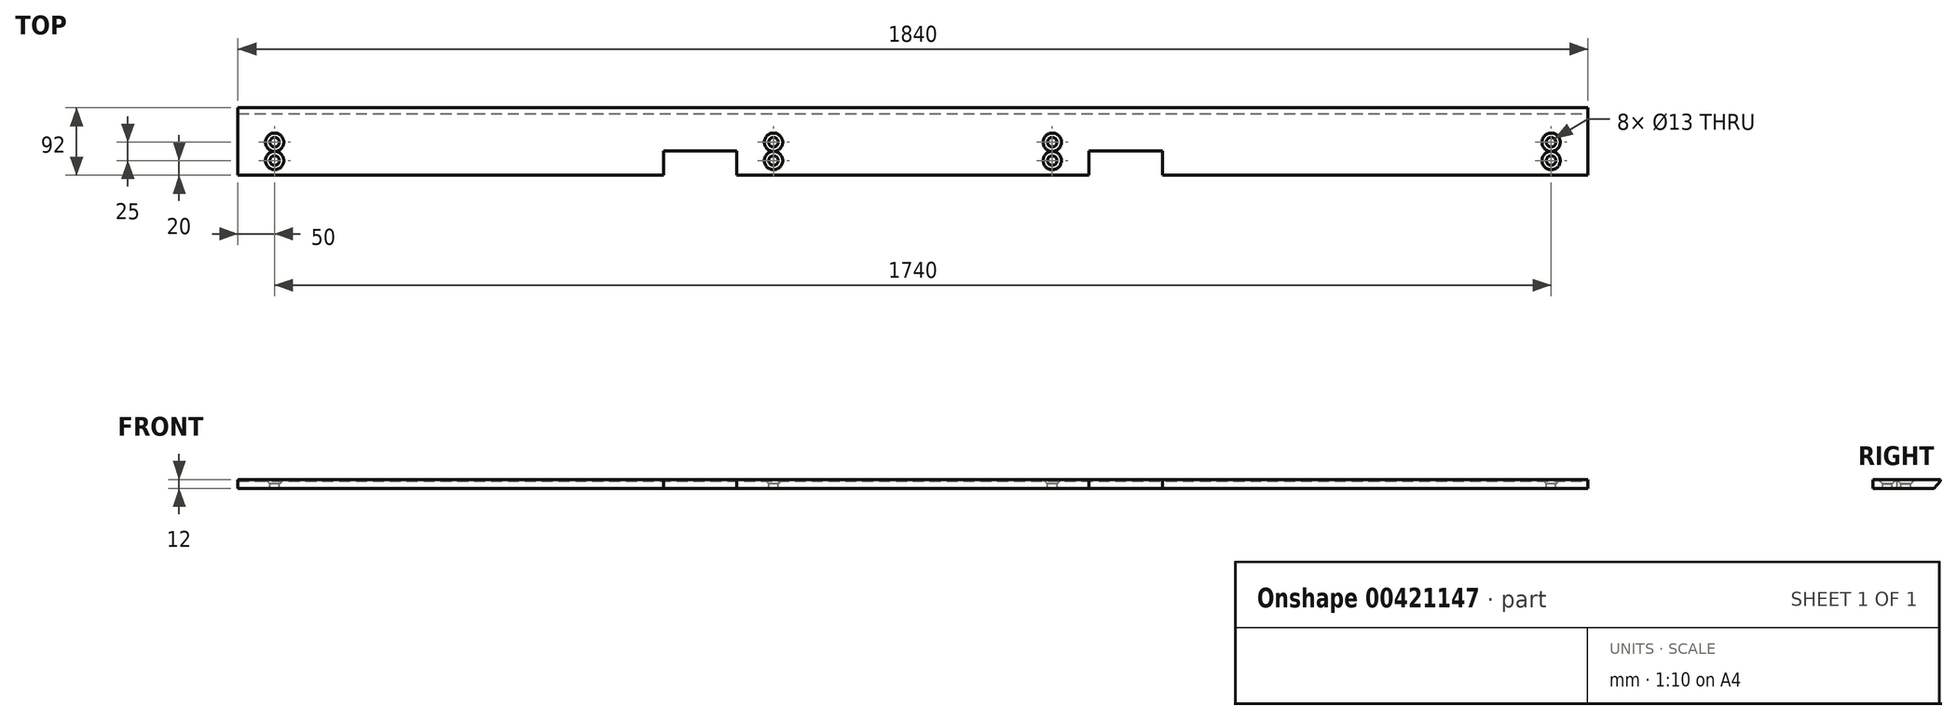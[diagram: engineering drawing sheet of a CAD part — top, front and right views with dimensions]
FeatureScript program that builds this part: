
annotation { "Feature Type Name" : "Feature", "Feature Type Description" : "" }
export const myFeature = defineFeature(function(context is Context, id is Id, definition is map)
    precondition{}
    {
        {
            var Q0;
            Q0=qCreatedBy(makeId("Top.planeOp"),FACE);
            var sketch = newSketch(context, id + "F0", { "sketchPlane" : qUnion([Q0])});
            skLineSegment(sketch, "E0.bottom", {"start": v(-920, 46) * mm, "end": v(920, 46) * mm});
            skLineSegment(sketch, "E0.top", {"start": v(-920, -46) * mm, "end": v(920, -46) * mm});
            skLineSegment(sketch, "E0.left", {"start": v(-920, 46) * mm, "end": v(-920, -46) * mm});
            skLineSegment(sketch, "E0.right", {"start": v(920, 46) * mm, "end": v(920, -46) * mm});
            skPoint(sketch, "E0.middle", {"position": v(0, 0) * mm});
            skSolve(sketch);
        }
        {
            var Q0;
            Q0=qSketchRegion(id+"F0",true);
            extrude(context, id + "F1", {"entities" : qUnion([Q0]), "endBound" : BoundingType.SYMMETRIC, "depth" : 12 * mm});
        }
        {
            var Q0;
            Q0=makeQuery(id+"F1.opExtrude","CAP_FACE",FACE,{"disambiguationData":[OSD([sQuery(id+"F0.wireOp",EDGE,"E0.bottom"),sQuery(id+"F0.wireOp",EDGE,"E0.top"),sQuery(id+"F0.wireOp",EDGE,"E0.left"),sQuery(id+"F0.wireOp",EDGE,"E0.right")])],"isStart":false});
            var sketch = newSketch(context, id + "F2", { "sketchPlane" : qUnion([Q0])});
            skLineSegment(sketch, "E1", {"start": v(0, 310.06) * mm, "end": v(0, -210.81) * mm, "construction": true});
            skLineSegment(sketch, "E2.0", {"start": v(-920, -46) * mm, "end": v(920, -46) * mm, "construction": true});
            skLineSegment(sketch, "E3.0", {"start": v(-240, 310.06) * mm, "end": v(-240, -210.81) * mm, "construction": true});
            skLineSegment(sketch, "E4.bottom", {"start": v(-240, -46) * mm, "end": v(-340, -46) * mm});
            skLineSegment(sketch, "E4.top", {"start": v(-240, -13) * mm, "end": v(-340, -13) * mm});
            skLineSegment(sketch, "E4.left", {"start": v(-240, -46) * mm, "end": v(-240, -13) * mm});
            skLineSegment(sketch, "E4.right", {"start": v(-340, -46) * mm, "end": v(-340, -13) * mm});
            skLineSegment(sketch, "E5.MirrorCS", {"start": v(340, -46) * mm, "end": v(340, -13) * mm});
            skLineSegment(sketch, "E6.MirrorCS", {"start": v(240, -46) * mm, "end": v(240, -13) * mm});
            skLineSegment(sketch, "E7.MirrorCS", {"start": v(240, -13) * mm, "end": v(340, -13) * mm});
            skLineSegment(sketch, "E8.MirrorCS", {"start": v(240, -46) * mm, "end": v(340, -46) * mm});
            skSolve(sketch);
        }
        {
            var Q0;
            Q0=qSketchRegion(id+"F2",true);
            extrude(context, id + "F3", {"entities" : qUnion([Q0]), "operationType" : NewBodyOperationType.REMOVE, "endBound" : BoundingType.THROUGH_ALL, "oppositeDirection" : true, "depth" : 25 * mm});
        }
        {
            var Q0;
            Q0=makeQuery(id+"F1.opExtrude","SWEPT_FACE",FACE,{"disambiguationData":[OSD([sQuery(id+"F0.wireOp",EDGE,"E0.right")])]});
            var sketch = newSketch(context, id + "F4", { "sketchPlane" : qUnion([Q0])});
            skLineSegment(sketch, "E9.0", {"start": v(46, 6) * mm, "end": v(-46, 6) * mm, "construction": true});
            skLineSegment(sketch, "E10.0", {"start": v(46, 4) * mm, "end": v(-46, 4) * mm, "construction": true});
            skLineSegment(sketch, "E11.0", {"start": v(46, 6) * mm, "end": v(46, -6) * mm, "construction": true});
            skLineSegment(sketch, "E12", {"start": v(46, 4) * mm, "end": v(37.6, -6) * mm});
            skLineSegment(sketch, "E13", {"start": v(46, 4) * mm, "end": v(46, -6) * mm});
            skLineSegment(sketch, "E14", {"start": v(46, -6) * mm, "end": v(37.6, -6) * mm});
            skSolve(sketch);
        }
        {
            var Q0;
            Q0=qSketchRegion(id+"F4",true);
            extrude(context, id + "F5", {"entities" : qUnion([Q0]), "operationType" : NewBodyOperationType.REMOVE, "endBound" : BoundingType.THROUGH_ALL, "oppositeDirection" : true, "depth" : 25 * mm});
        }
        {
            var Q0;
            Q0=makeQuery(id+"F1.opExtrude","CAP_FACE",FACE,{"disambiguationData":[OSD([sQuery(id+"F0.wireOp",EDGE,"E0.bottom"),sQuery(id+"F0.wireOp",EDGE,"E0.top"),sQuery(id+"F0.wireOp",EDGE,"E0.left"),sQuery(id+"F0.wireOp",EDGE,"E0.right")])],"isStart":false});
            var sketch = newSketch(context, id + "F6", { "sketchPlane" : qUnion([Q0])});
            skLineSegment(sketch, "E15", {"start": v(0, 160.59) * mm, "end": v(0, -190.3) * mm, "construction": true});
            skLineSegment(sketch, "E16.0", {"start": v(-190, 160.59) * mm, "end": v(-190, -190.3) * mm, "construction": true});
            skLineSegment(sketch, "E17.0", {"start": v(-870, 160.59) * mm, "end": v(-870, -190.3) * mm, "construction": true});
            skLineSegment(sketch, "E18.0", {"start": v(-920, -46) * mm, "end": v(0, -46) * mm, "construction": true});
            skPoint(sketch, "E19.orphan", {"position": v(-340, -46) * mm});
            skLineSegment(sketch, "E20.0", {"start": v(-920, -26) * mm, "end": v(0, -26) * mm, "construction": true});
            skLineSegment(sketch, "E21.0", {"start": v(-920, -1) * mm, "end": v(0, -1) * mm, "construction": true});
            skPoint(sketch, "E22", {"position": v(-870, -1) * mm});
            skPoint(sketch, "E23", {"position": v(-870, -26) * mm});
            skPoint(sketch, "E24", {"position": v(-190, -1) * mm});
            skPoint(sketch, "E25", {"position": v(-190, -26) * mm});
            skPoint(sketch, "E26.MirrorP", {"position": v(870, -1) * mm});
            skPoint(sketch, "E27.MirrorP", {"position": v(870, -26) * mm});
            skPoint(sketch, "E28.MirrorP", {"position": v(190, -1) * mm});
            skPoint(sketch, "E29.MirrorP", {"position": v(190, -26) * mm});
            skSolve(sketch);
        }
        {
            var Q0;
            Q0=sQuery(id+"F6.wireOp",VERTEX,"E22");
            var Q1;
            Q1=sQuery(id+"F6.wireOp",VERTEX,"E23");
            var Q2;
            Q2=sQuery(id+"F6.wireOp",VERTEX,"E24");
            var Q3;
            Q3=sQuery(id+"F6.wireOp",VERTEX,"E25");
            var Q4;
            Q4=sQuery(id+"F6.wireOp",VERTEX,"E29.MirrorP");
            var Q5;
            Q5=sQuery(id+"F6.wireOp",VERTEX,"E28.MirrorP");
            var Q6;
            Q6=sQuery(id+"F6.wireOp",VERTEX,"E26.MirrorP");
            var Q7;
            Q7=sQuery(id+"F6.wireOp",VERTEX,"E27.MirrorP");
            var Q8;
            Q8=makeQuery(id+"F1.opExtrude","SWEPT_BODY",BODY,{"disambiguationData":[OSD([sQuery(id+"F0.wireOp",EDGE,"E0.bottom"),sQuery(id+"F0.wireOp",EDGE,"E0.top"),sQuery(id+"F0.wireOp",EDGE,"E0.left"),sQuery(id+"F0.wireOp",EDGE,"E0.right")])]});
            hole(context, id + "F7", {"style" : HoleStyle.C_SINK, "endStyle" : HoleEndStyle.THROUGH, "holeDiameter" : 13 * mm, "cSinkDiameter" : 25 * mm, "cSinkAngle" : 90 * degree, "locations" : qUnion([Q0, Q1, Q2, Q3, Q4, Q5, Q6, Q7]), "scope" : qUnion([Q8]), "isTappedThrough" : true});
        }
    });
